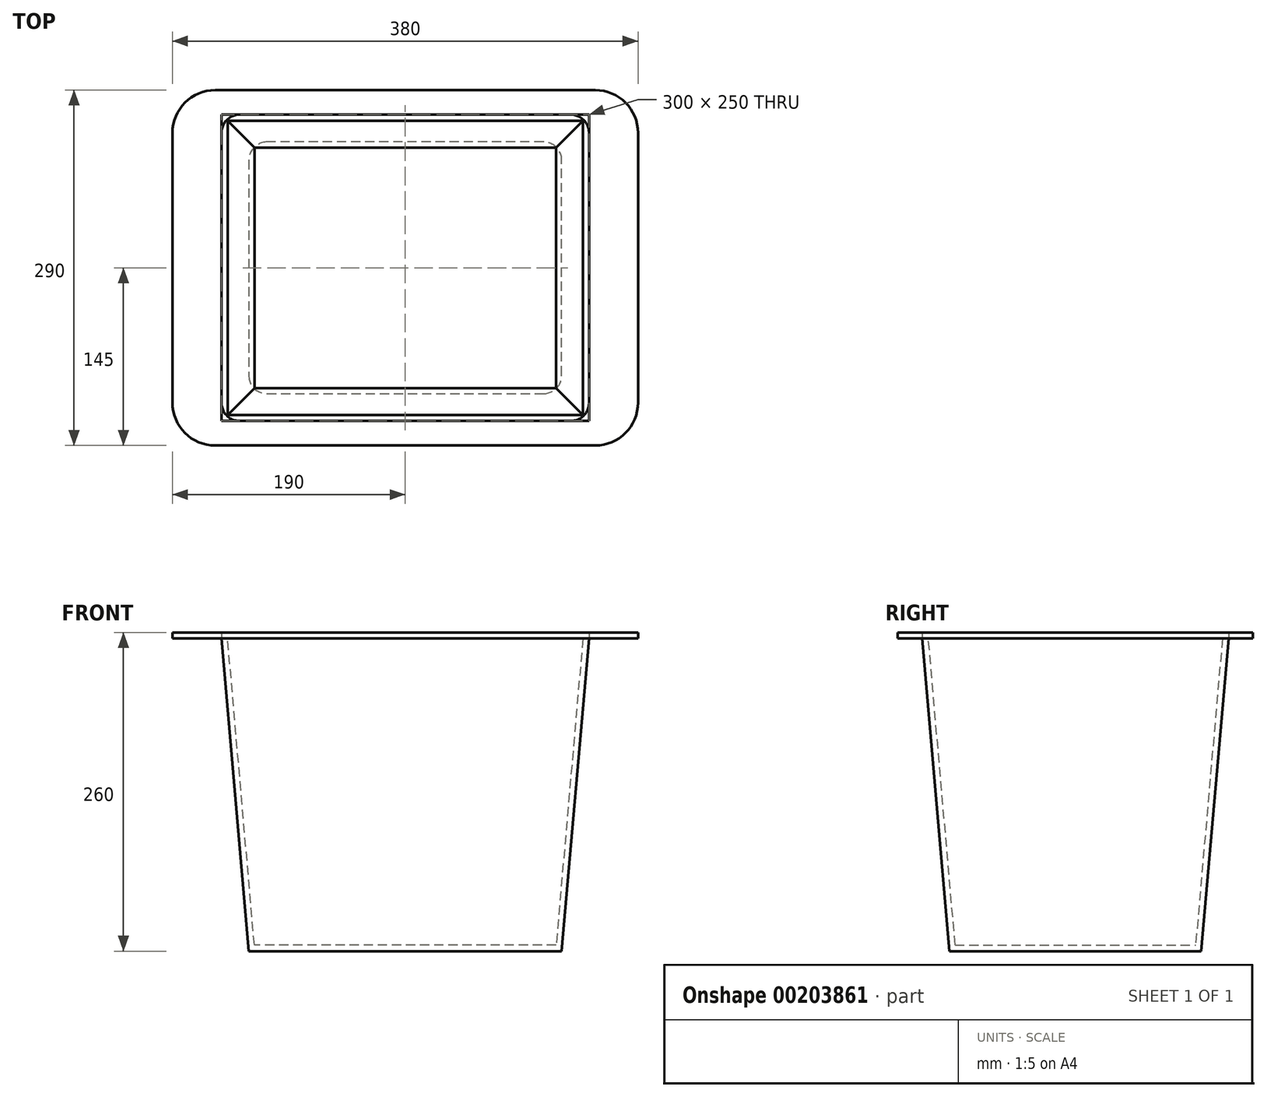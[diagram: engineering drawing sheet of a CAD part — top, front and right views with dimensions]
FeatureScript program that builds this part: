
annotation { "Feature Type Name" : "Feature", "Feature Type Description" : "" }
export const myFeature = defineFeature(function(context is Context, id is Id, definition is map)
    precondition{}
    {
        {
            var Q0;
            Q0=qCreatedBy(makeId("Top.planeOp"),FACE);
            var sketch = newSketch(context, id + "F0", { "sketchPlane" : qUnion([Q0])});
            skPoint(sketch, "E0.middle", {"position": v(0, 0) * mm});
            skLineSegment(sketch, "E1.bottom", {"start": v(150, 125) * mm, "end": v(-150, 125) * mm});
            skLineSegment(sketch, "E1.top", {"start": v(150, -125) * mm, "end": v(-150, -125) * mm});
            skLineSegment(sketch, "E1.left", {"start": v(150, 125) * mm, "end": v(150, -125) * mm});
            skLineSegment(sketch, "E1.right", {"start": v(-150, 125) * mm, "end": v(-150, -125) * mm});
            skSolve(sketch);
        }
        {
            var Q0;
            Q0 = qSketchRegion(id + "F0", true);
            extrude(context, id + "F1", {"entities" : qUnion([Q0]), "oppositeDirection" : true, "depth" : 255 * mm, "hasDraft" : true, "draftAngle" : 5 * degree, "draftPullDirection" : true});
        }
        {
            var Q0;
            Q0=makeQuery(id+"F1.opExtrude","CAP_FACE",FACE,{"disambiguationData":[OSD([sQuery(id+"F0.wireOp",EDGE,"E1.bottom"),sQuery(id+"F0.wireOp",EDGE,"E1.top"),sQuery(id+"F0.wireOp",EDGE,"E1.left"),sQuery(id+"F0.wireOp",EDGE,"E1.right")])],"isStart":true});
            shell(context, id + "F2", {"entities" : qUnion([Q0]), "thickness" : 5 * mm});
        }
        {
            var Q0;
            Q0=makeQuery(id+"F1.opExtrude","CAP_FACE",FACE,{"disambiguationData":[OSD([sQuery(id+"F0.wireOp",EDGE,"E1.bottom"),sQuery(id+"F0.wireOp",EDGE,"E1.top"),sQuery(id+"F0.wireOp",EDGE,"E1.left"),sQuery(id+"F0.wireOp",EDGE,"E1.right")])],"isStart":true});
            var sketch = newSketch(context, id + "F3", { "sketchPlane" : qUnion([Q0])});
            skLineSegment(sketch, "E2.bottom", {"start": v(155, 145) * mm, "end": v(-155, 145) * mm});
            skLineSegment(sketch, "E2.top", {"start": v(155, -145) * mm, "end": v(-155, -145) * mm});
            skLineSegment(sketch, "E2.left", {"start": v(190, 110) * mm, "end": v(190, -110) * mm});
            skLineSegment(sketch, "E2.right", {"start": v(-190, 110) * mm, "end": v(-190, -110) * mm});
            skPoint(sketch, "E2.middle", {"position": v(0, 0) * mm});
            skLineSegment(sketch, "E3.bottom", {"start": v(150, 125) * mm, "end": v(-150, 125) * mm});
            skLineSegment(sketch, "E3.top", {"start": v(150, -125) * mm, "end": v(-150, -125) * mm});
            skLineSegment(sketch, "E3.left", {"start": v(150, 125) * mm, "end": v(150, -125) * mm});
            skLineSegment(sketch, "E3.right", {"start": v(-150, 125) * mm, "end": v(-150, -125) * mm});
            skPoint(sketch, "E4.visualSharp", {"position": v(-190, -145) * mm});
            skArc(sketch, "E4.filletArc", {"start": v(-190, -110) * mm, "mid": v(-179.75, -134.75) * mm, "end": v(-155, -145) * mm});
            skPoint(sketch, "E5.visualSharp", {"position": v(-190, 145) * mm});
            skArc(sketch, "E5.filletArc", {"start": v(-155, 145) * mm, "mid": v(-179.75, 134.75) * mm, "end": v(-190, 110) * mm});
            skPoint(sketch, "E6.visualSharp", {"position": v(190, 145) * mm});
            skArc(sketch, "E6.filletArc", {"start": v(190, 110) * mm, "mid": v(179.75, 134.75) * mm, "end": v(155, 145) * mm});
            skPoint(sketch, "E7.visualSharp", {"position": v(190, -145) * mm});
            skArc(sketch, "E7.filletArc", {"start": v(155, -145) * mm, "mid": v(179.75, -134.75) * mm, "end": v(190, -110) * mm});
            skSolve(sketch);
        }
        {
            var Q0;
            Q0 = qSketchRegion(id + "F3", true);
            extrude(context, id + "F4", {"entities" : qUnion([Q0]), "depth" : 5 * mm});
        }
        {
            var Q0;
            Q0=makeQuery(id+"F1.opExtrude","SWEPT_EDGE",EDGE,{"disambiguationData":[OSD([sQuery(id+"F0.wireOp",EDGE,"E1.bottom"),sQuery(id+"F0.wireOp",EDGE,"E1.right")])]});
            var Q1;
            Q1=makeQuery(id+"F1.opExtrude","SWEPT_EDGE",EDGE,{"disambiguationData":[OSD([sQuery(id+"F0.wireOp",EDGE,"E1.top"),sQuery(id+"F0.wireOp",EDGE,"E1.right")])]});
            var Q2;
            Q2=makeQuery(id+"F1.opExtrude","SWEPT_EDGE",EDGE,{"disambiguationData":[OSD([sQuery(id+"F0.wireOp",EDGE,"E1.top"),sQuery(id+"F0.wireOp",EDGE,"E1.left")])]});
            var Q3;
            Q3=makeQuery(id+"F1.opExtrude","SWEPT_EDGE",EDGE,{"disambiguationData":[OSD([sQuery(id+"F0.wireOp",EDGE,"E1.bottom"),sQuery(id+"F0.wireOp",EDGE,"E1.left")])]});
            fillet(context, id + "F5", {"entities" : qUnion([Q0, Q1, Q2, Q3]), "radius" : 15 * mm, "tangentPropagation" : true, "allowEdgeOverflow" : false});
        }
    });
